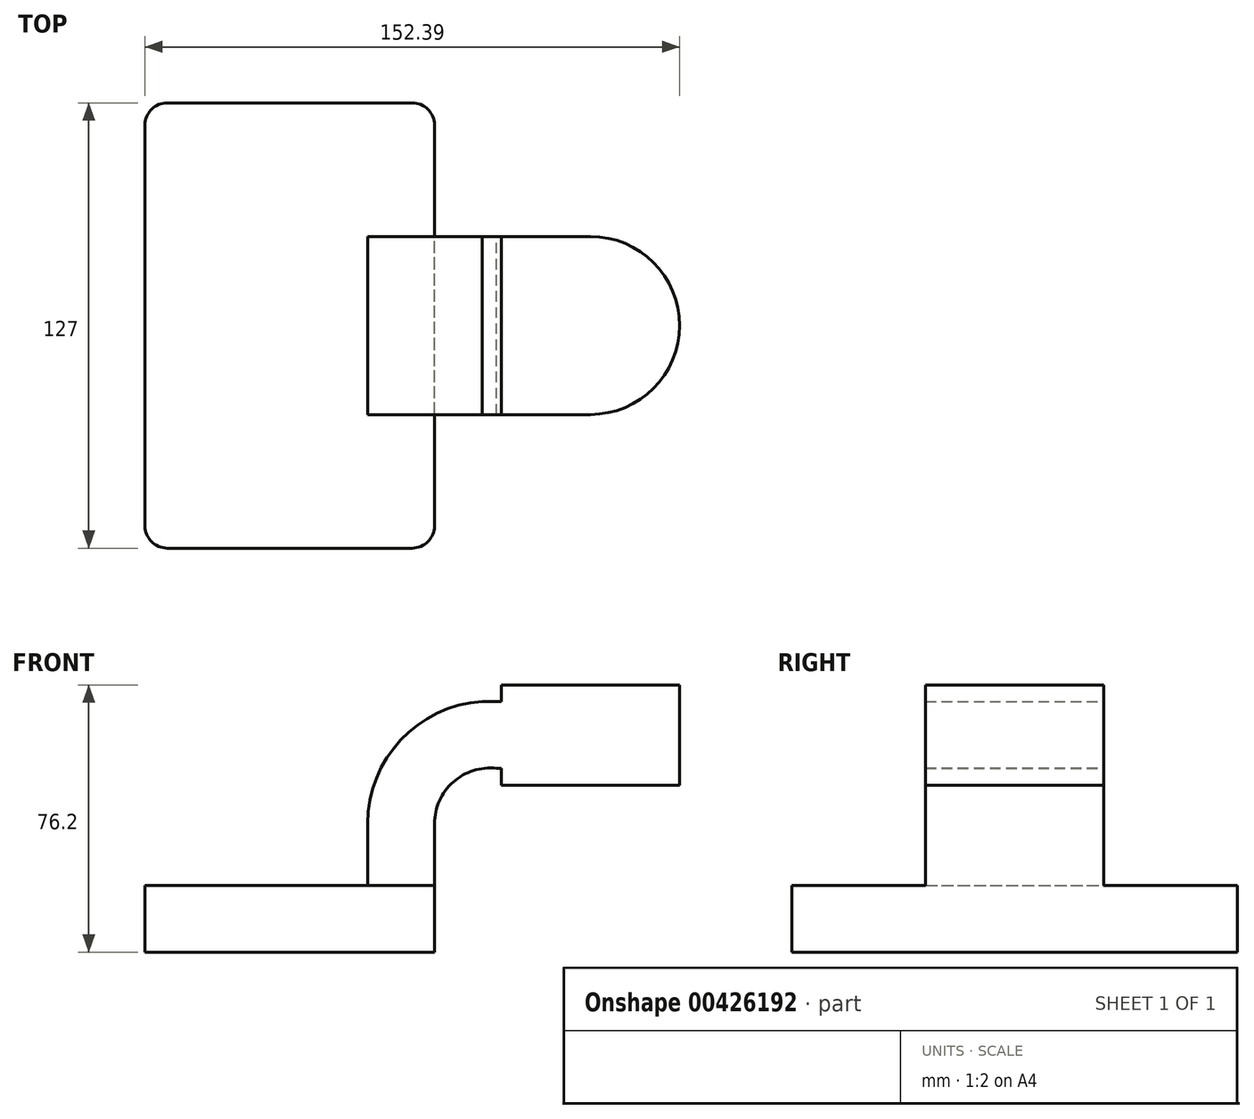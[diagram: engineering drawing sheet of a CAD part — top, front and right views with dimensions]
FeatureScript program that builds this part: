
annotation { "Feature Type Name" : "Feature", "Feature Type Description" : "" }
export const myFeature = defineFeature(function(context is Context, id is Id, definition is map)
    precondition{}
    {
        {
            var Q0;
            Q0=qCreatedBy(makeId("Front.planeOp"),FACE);
            var sketch = newSketch(context, id + "F0", { "sketchPlane" : qUnion([Q0])});
            skLineSegment(sketch, "E0.bottom", {"start": v(-41.28, -9.53) * mm, "end": v(41.28, -9.53) * mm});
            skLineSegment(sketch, "E0.top", {"start": v(-41.28, 9.53) * mm, "end": v(41.28, 9.53) * mm});
            skLineSegment(sketch, "E0.left", {"start": v(-41.28, -9.53) * mm, "end": v(-41.28, 9.53) * mm});
            skLineSegment(sketch, "E0.right", {"start": v(41.28, -9.53) * mm, "end": v(41.28, 9.52) * mm});
            skPoint(sketch, "E0.middle", {"position": v(0, 0) * mm});
            skLineSegment(sketch, "E1.bottom", {"start": v(111.12, 38.1) * mm, "end": v(60.32, 38.1) * mm});
            skLineSegment(sketch, "E1.top", {"start": v(111.12, 66.68) * mm, "end": v(60.32, 66.68) * mm});
            skLineSegment(sketch, "E1.left", {"start": v(111.12, 38.1) * mm, "end": v(111.12, 66.68) * mm});
            skLineSegment(sketch, "E1.right", {"start": v(60.32, 38.1) * mm, "end": v(60.32, 66.68) * mm});
            skPoint(sketch, "E1.middle", {"position": v(85.72, 52.39) * mm});
            skLineSegment(sketch, "E2", {"start": v(41.28, 9.52) * mm, "end": v(41.28, 27.1) * mm});
            skArc(sketch, "E3", {"start": v(41.28, 27.1) * mm, "mid": v(46.58, 38.95) * mm, "end": v(58.95, 42.88) * mm});
            skLineSegment(sketch, "E4", {"start": v(58.95, 42.88) * mm, "end": v(85.72, 42.88) * mm});
            skArc(sketch, "E5.0", {"start": v(22.23, 27.1) * mm, "mid": v(31.64, 50.96) * mm, "end": v(54.82, 61.95) * mm});
            skLineSegment(sketch, "E5.1", {"start": v(22.22, 9.52) * mm, "end": v(22.22, 27.1) * mm});
            skLineSegment(sketch, "E6", {"start": v(54.82, 61.95) * mm, "end": v(85.72, 61.95) * mm});
            skLineSegment(sketch, "E7", {"start": v(85.72, 66.68) * mm, "end": v(85.72, 38.1) * mm});
            skFitSpline(sketch, "E8", {"points": [v(-41.28, 9.52) * mm, v(54.82, 61.95) * mm], "startDerivative": vector(55.67, 107.04) * mm, "endDerivative": vector(112.6, -3.11) * mm});
            skSolve(sketch);
        }
        {
            var Q0;
            Q0=makeQuery(id+"F0.imprint","IMPRINT",FACE,{"disambiguationData":[TD([[makeQuery(id+"F0.imprint","IMPRINT",EDGE,{"derivedFrom":sQuery(id+"F0.wireOp",EDGE,"E0.bottom")}),1.0]])]});
            extrude(context, id + "F1", {"entities" : qUnion([Q0]), "endBound" : BoundingType.SYMMETRIC, "depth" : 127 * mm});
        }
        {
            var Q0;
            Q0=makeQuery(id+"F0.imprint","IMPRINT",FACE,{"disambiguationData":[TD([[makeQuery(id+"F0.imprint","IMPRINT",EDGE,{"derivedFrom":sQuery(id+"F0.wireOp",EDGE,"E0.bottom")}),1.0]])]});
            var Q1;
            {var subQ0=sQuery(id+"F0.wireOp",EDGE,"E1.right");var subQ1=sQuery(id+"F0.wireOp",EDGE,"E1.bottom");var subQ2=makeQuery(id+"F0.imprint","INTERSECT",VERTEX,{"derivedFrom":[subQ1,subQ0]});Q1=makeQuery(id+"F0.imprint","IMPRINT",FACE,{"disambiguationData":[TD([[makeQuery(id+"F0.imprint","IMPRINT",EDGE,{"disambiguationData":[TD([[subQ2,1.0]])],"derivedFrom":subQ1}),-1.0]])]});}
            var Q2;
            {var subQ0=sQuery(id+"F0.wireOp",EDGE,"E1.right");var subQ1=sQuery(id+"F0.wireOp",EDGE,"E1.top");var subQ2=makeQuery(id+"F0.imprint","INTERSECT",VERTEX,{"derivedFrom":[subQ1,subQ0]});Q2=makeQuery(id+"F0.imprint","IMPRINT",FACE,{"disambiguationData":[TD([[makeQuery(id+"F0.imprint","IMPRINT",EDGE,{"disambiguationData":[TD([[subQ2,1.0]])],"derivedFrom":subQ1}),1.0]])]});}
            var Q3;
            {var subQ1=sQuery(id+"F0.wireOp",EDGE,"E2");Q3=makeQuery(id+"F0.imprint","IMPRINT",FACE,{"disambiguationData":[TD([[makeQuery(id+"F0.imprint","IMPRINT",EDGE,{"derivedFrom":subQ1}),1.0]])]});}
            var Q4;
            {var subQ0=sQuery(id+"F0.wireOp",EDGE,"E4");var subQ1=sQuery(id+"F0.wireOp",EDGE,"E1.right");var subQ2=makeQuery(id+"F0.imprint","INTERSECT",VERTEX,{"derivedFrom":[subQ1,subQ0]});Q4=makeQuery(id+"F0.imprint","IMPRINT",FACE,{"disambiguationData":[TD([[makeQuery(id+"F0.imprint","IMPRINT",EDGE,{"disambiguationData":[TD([[subQ2,-1.0]])],"derivedFrom":subQ1}),-1.0]])]});}
            extrude(context, id + "F2", {"entities" : qUnion([Q0, Q1, Q2, Q3, Q4]), "operationType" : NewBodyOperationType.ADD, "endBound" : BoundingType.SYMMETRIC, "depth" : 50.8 * mm});
        }
        {
            var Q0;
            Q0=makeQuery(id+"F0.imprint","IMPRINT",FACE,{"disambiguationData":[TD([[makeQuery(id+"F0.imprint","IMPRINT",EDGE,{"derivedFrom":sQuery(id+"F0.wireOp",EDGE,"E5.0")}),1.0]])]});
            extrude(context, id + "F3", {"entities" : qUnion([Q0]), "operationType" : NewBodyOperationType.ADD, "endBound" : BoundingType.SYMMETRIC, "depth" : 15.88 * mm});
        }
        {
            var Q0;
            {var subQ4=sQuery(id+"F0.wireOp",EDGE,"E1.left");Q0=makeQuery(id+"F0.imprint","IMPRINT",FACE,{"disambiguationData":[TD([[makeQuery(id+"F0.imprint","IMPRINT",EDGE,{"derivedFrom":subQ4}),1.0]])]});}
            var Q1;
            Q1=sQuery(id+"F0.wireOp",EDGE,"E7");
            revolve(context, id + "F4", {"operationType" : NewBodyOperationType.ADD, "entities" : qUnion([Q0]), "axis" : qUnion([Q1]), "revolveType" : RevolveType.FULL});
        }
        {
            var Q0;
            Q0=makeQuery(id+"F1.opExtrude","CAP_EDGE",EDGE,{"disambiguationData":[OSD([sQuery(id+"F0.wireOp",EDGE,"E0.right")])],"isStart":false});
            var Q1;
            Q1=makeQuery(id+"F1.opExtrude","CAP_EDGE",EDGE,{"disambiguationData":[OSD([sQuery(id+"F0.wireOp",EDGE,"E0.left")])],"isStart":false});
            var Q2;
            Q2=makeQuery(id+"F1.opExtrude","CAP_EDGE",EDGE,{"disambiguationData":[OSD([sQuery(id+"F0.wireOp",EDGE,"E0.left")])],"isStart":true});
            var Q3;
            Q3=makeQuery(id+"F1.opExtrude","CAP_EDGE",EDGE,{"disambiguationData":[OSD([sQuery(id+"F0.wireOp",EDGE,"E0.right")])],"isStart":true});
            fillet(context, id + "F5", {"entities" : qUnion([Q0, Q1, Q2, Q3]), "radius" : 6.35 * mm, "tangentPropagation" : true, "allowEdgeOverflow" : false});
        }
    });
